# Revit family: Kombiventil 4006_M
name_source: partatom
category: Rohrzubehör
revit_build: Autodesk Revit 2018 (Build: 20190510_1515(x64)
units: mm (PartAtom-declared; Revit-internal decimal feet)

## family parameters
Arbeitsebenenbasiert = Nein
Beim Laden mit Abzugskörper schneiden = Nein
Bemaßung runder Anschluss = Durchmesser verwenden
Gemeinsam genutzt = Nein
Immer vertikal = Ja
OmniClass-Nummer = 23.65.55.14
OmniClass-Titel = Valves for Liquid Services
Teiletyp = Unterbricht

## types (1)
- Kombiventil 4006_M
    Anwendungsgebiet = Das Kombiventil wird in allen pumpenbetriebenen Heiz- und Kühlanlagen eingesetzt. Der Regler begrenzt automatisch
den Volumenstrom im gewählten Anlagenteil auf den einmal eingestellten Wert, indem alle Druckschwankungen
gemessen und ausgeregelt werden. Somit sind keine Messungen erforderlich und die Regelung ist bei allen
Betriebsbedingungen effektiv. Das Kombiventil regelt den Volumenstrom der ventileigenen Voreinstellung auf einen
konstanten Wert; die Membran regelt aufgrund des Druckes unmittelbar nach dem Regeleinsatz, sowie des Druckes
davor.
Die Verwendung von Ethylen- und Propylenglykol ist im Mischungsverhältnis 25 - 50 Vol.- [%] zulässig.
    Bauschutzkappe = Kunststoff
    Druckfeder = Federstahl
    Gehäuse = DZR Messing CC770S
    H05 = 9 mm  [stored 0.0295276 ft]
    H07 = 4 mm  [stored 0.0131234 ft]
    H09 = 21.8 mm  [stored 0.0715223 ft]
    H12 = 19.25 mm  [stored 0.0631562 ft]
    Hersteller = Herz-Armaturen GmbH
    Hub = 4 mm  [stored 0.0131234 ft]
    Impulsleitung = Kupfer Cu-DHP (CW024A)
    L02 = 43.5 mm  [stored 0.142717 ft]
    L03 = 3.2 mm  [stored 0.0104987 ft]
    L04 = 1.5 mm  [stored 0.00492126 ft]
    L05 = 11 mm  [stored 0.0360892 ft]
    Medium = Heizungswasserqualität nach ÖNORM H 5195 oder VDI-Richtline 2035.
Die Verwendung von Ethylen- oder
Propylenglykol in einem Mischungsverhältnis 25 - 50% ist zulässig.
    Membrane = EPDM
    Membrangehäuse = Messing CW602N
    O-Ringe = EPDM
    PN = 16
    R04 = 12.5 mm  [stored 0.0410105 ft]
    R05 = 15 mm  [stored 0.0492126 ft]
    R08 = 11.3 mm  [stored 0.0370735 ft]
    R09 = 18.25 mm  [stored 0.0598753 ft]
    R10 = 35 mm  [stored 0.114829 ft]
    R11 = 6.5 mm
    R12 = 3.9 mm  [stored 0.0127953 ft]
    SCRNCODE = 05;04;02
    SCRNSEQ = ARM;ARM_TYP="DURR";2
    Stift = Edelstahl 14301
    URL = www.herz-armaturen.at
    VRL02 = 18 mm  [stored 0.0590551 ft]
    VRL04 = 8 mm  [stored 0.0262467 ft]
    max.Betriebsdruck = 1600000.0 Pa
    max.Betriebstemperatur ab DN40 = 110 °C
    max.Betriebstemperatur bis DN32 = 130 °C
    min.Betriebstemperatur (Frostschutz) = -20 °C
    min.Betriebstemperatur (reines Wasser) = 2 °C

note: [stored X ft] marks values corroborated as IEEE doubles in the binary element streams (Revit-internal decimal feet)
